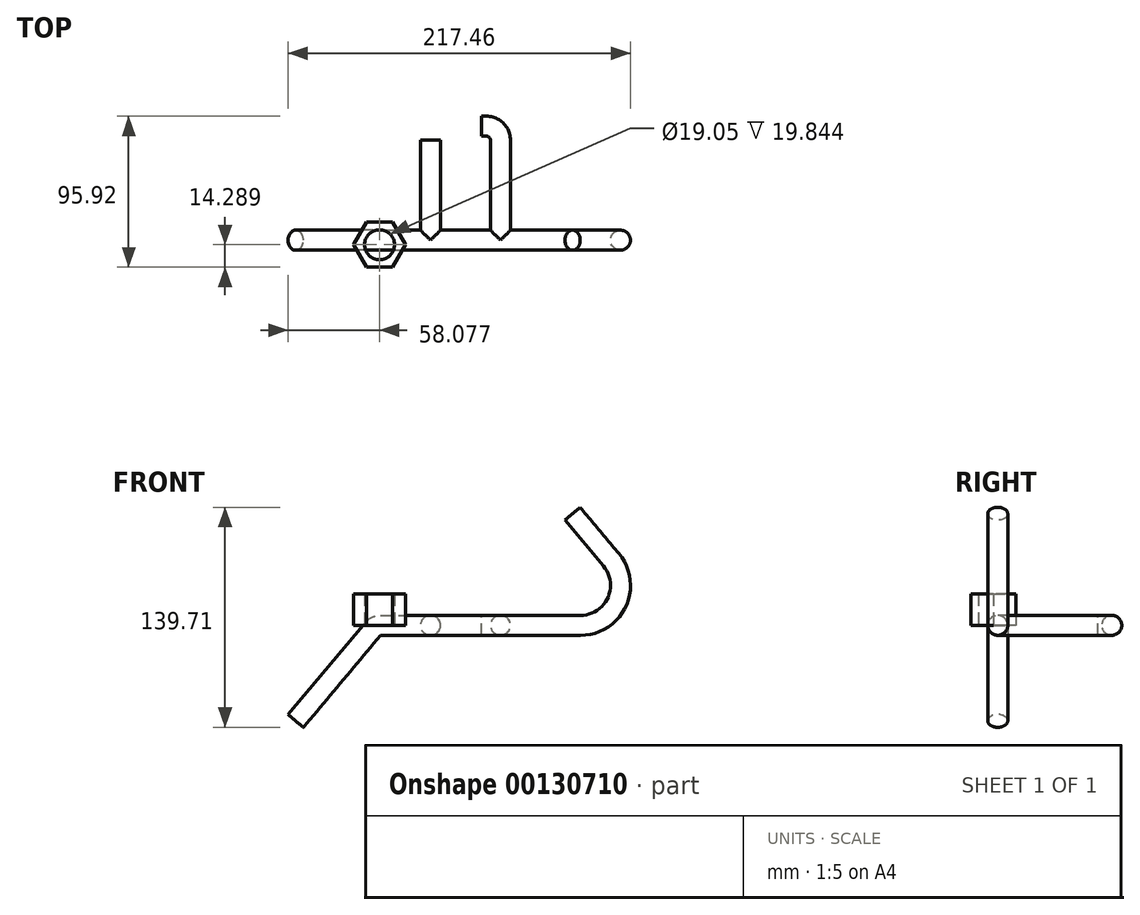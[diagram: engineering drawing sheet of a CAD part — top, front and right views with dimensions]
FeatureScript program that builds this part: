
annotation { "Feature Type Name" : "Feature", "Feature Type Description" : "" }
export const myFeature = defineFeature(function(context is Context, id is Id, definition is map)
    precondition{}
    {
        {
            var Q0;
            Q0=qCreatedBy(makeId("Front.planeOp"),FACE);
            var sketch = newSketch(context, id + "F0", { "sketchPlane" : qUnion([Q0])});
            skLineSegment(sketch, "E0", {"start": v(0, 0) * mm, "end": v(120.65, 0) * mm});
            skLineSegment(sketch, "E1", {"start": v(115.62, 70.91) * mm, "end": v(140.1, 41.73) * mm});
            skArc(sketch, "E2", {"start": v(120.65, 0) * mm, "mid": v(143.67, 14.67) * mm, "end": v(140.1, 41.73) * mm});
            skLineSegment(sketch, "E3", {"start": v(0, 0) * mm, "end": v(0, 0) * mm});
            skLineSegment(sketch, "E4", {"start": v(-11.21, -2.27) * mm, "end": v(-60.2, -60.64) * mm});
            skPoint(sketch, "E5.visualSharp", {"position": v(-9.31, 0) * mm});
            skArc(sketch, "E5.filletArc", {"start": v(-6.35, 0) * mm, "mid": v(-9.03, -0.6) * mm, "end": v(-11.21, -2.27) * mm});
            skLineSegment(sketch, "E6", {"start": v(-6.35, 0) * mm, "end": v(0, 0) * mm});
            skSolve(sketch);
        }
        {
            var Q0;
            Q0=qCreatedBy(makeId("Right.planeOp"),FACE);
            var sketch = newSketch(context, id + "F1", { "sketchPlane" : qUnion([Q0])});
            skCircle(sketch, "E7", {"center": v(0, 0) * mm, "radius": 6.35 * mm});
            skSolve(sketch);
        }
        {
            var Q0;
            Q0 = qSketchRegion(id + "F1", true);
            var Q1;
            Q1=sQuery(id+"F0.wireOp",EDGE,"E0");
            var Q2;
            Q2=sQuery(id+"F0.wireOp",EDGE,"E2");
            var Q3;
            Q3=sQuery(id+"F0.wireOp",EDGE,"E1");
            sweep(context, id + "F2", {"profiles" : qUnion([Q0]), "path" : qUnion([Q1, Q2, Q3])});
        }
        {
            var Q0;
            Q0 = qSketchRegion(id + "F1", true);
            var Q1;
            Q1=sQuery(id+"F0.wireOp",EDGE,"E6");
            var Q2;
            Q2=sQuery(id+"F0.wireOp",EDGE,"E5.filletArc");
            var Q3;
            Q3=sQuery(id+"F0.wireOp",EDGE,"E4");
            sweep(context, id + "F3", {"operationType" : NewBodyOperationType.ADD, "profiles" : qUnion([Q0]), "path" : qUnion([Q1, Q2, Q3])});
        }
        {
            var Q0;
            Q0=qCreatedBy(makeId("Front.planeOp"),FACE);
            var sketch = newSketch(context, id + "F4", { "sketchPlane" : qUnion([Q0])});
            skCircle(sketch, "E8", {"center": v(25.4, 0) * mm, "radius": 6.35 * mm});
            skCircle(sketch, "E9", {"center": v(69.85, 0) * mm, "radius": 6.35 * mm});
            skSolve(sketch);
        }
        {
            var Q0;
            Q0 = qSketchRegion(id + "F4", true);
            var Q1;
            Q1=sQuery(id+"F4.wireOp",EDGE,"E8");
            extrude(context, id + "F5", {"entities" : qUnion([Q0]), "operationType" : NewBodyOperationType.ADD, "surfaceEntities" : qUnion([Q1]), "oppositeDirection" : true, "depth" : 63.5 * mm});
        }
        {
            var Q0;
            Q0=qCreatedBy(makeId("Top.planeOp"),FACE);
            var sketch = newSketch(context, id + "F6", { "sketchPlane" : qUnion([Q0])});
            skLineSegment(sketch, "E10.0.0", {"start": v(63.5, 63.5) * mm, "end": v(76.2, 63.5) * mm, "construction": true});
            skArc(sketch, "E11", {"start": v(69.85, 63.5) * mm, "mid": v(67.25, 69.79) * mm, "end": v(60.96, 72.39) * mm});
            skLineSegment(sketch, "E12", {"start": v(69.85, 63.5) * mm, "end": v(69.85, 58.55) * mm, "construction": true});
            skLineSegment(sketch, "E13", {"start": v(60.96, 72.4) * mm, "end": v(57.79, 72.4) * mm});
            skSolve(sketch);
        }
        {
            var Q0;
            Q0=makeQuery(id+"F5.opExtrude","CAP_FACE",FACE,{"disambiguationData":[OSD([sQuery(id+"F4.wireOp",EDGE,"E9")])],"isStart":false});
            var Q1;
            Q1=sQuery(id+"F6.wireOp",EDGE,"E11");
            var Q2;
            Q2=sQuery(id+"F6.wireOp",EDGE,"E13");
            sweep(context, id + "F7", {"operationType" : NewBodyOperationType.ADD, "profiles" : qUnion([Q0]), "path" : qUnion([Q1, Q2])});
        }
        {
            var Q0;
            Q0=qCreatedBy(makeId("Top.planeOp"),FACE);
            var sketch = newSketch(context, id + "F8", { "sketchPlane" : qUnion([Q0])});
            skCircle(sketch, "E14.cCircle", {"center": v(-6.98, -2.9) * mm, "radius": 14.29 * mm, "construction": true});
            skLineSegment(sketch, "E14.0", {"start": v(1.27, 11.4) * mm, "end": v(9.51, -2.9) * mm});
            skLineSegment(sketch, "E14.1", {"start": v(9.51, -2.9) * mm, "end": v(1.27, -17.18) * mm});
            skLineSegment(sketch, "E14.2", {"start": v(1.27, -17.18) * mm, "end": v(-15.23, -17.18) * mm});
            skLineSegment(sketch, "E14.3", {"start": v(-15.23, -17.18) * mm, "end": v(-23.48, -2.9) * mm});
            skLineSegment(sketch, "E14.4", {"start": v(-23.48, -2.9) * mm, "end": v(-15.23, 11.4) * mm});
            skLineSegment(sketch, "E14.5", {"start": v(-15.23, 11.4) * mm, "end": v(1.27, 11.4) * mm});
            skPoint(sketch, "E14.0.midPoint", {"position": v(5.4, 4.25) * mm});
            skCircle(sketch, "E15", {"center": v(-6.98, -2.9) * mm, "radius": 9.53 * mm});
            skSolve(sketch);
        }
        {
            var Q0;
            Q0=makeQuery(id+"F8.imprint","IMPRINT",FACE,{"disambiguationData":[TD([[makeQuery(id+"F8.imprint","IMPRINT",EDGE,{"derivedFrom":sQuery(id+"F8.wireOp",EDGE,"E14.0")}),-1.0]])]});
            extrude(context, id + "F9", {"entities" : qUnion([Q0]), "depth" : 19.84 * mm});
        }
    });
